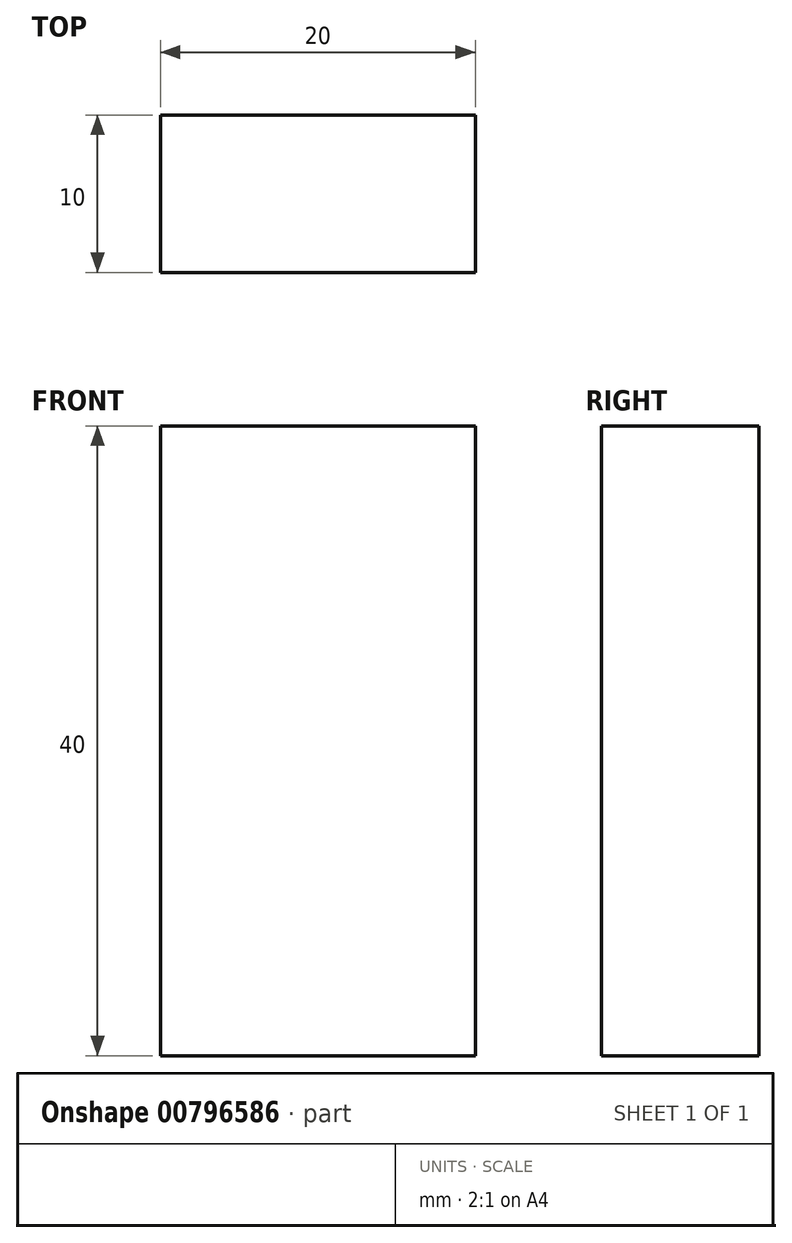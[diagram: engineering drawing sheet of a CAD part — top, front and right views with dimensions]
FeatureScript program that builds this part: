
annotation { "Feature Type Name" : "Feature", "Feature Type Description" : "" }
export const myFeature = defineFeature(function(context is Context, id is Id, definition is map)
    precondition{}
    {
        {
            var Q0;
            Q0=qCreatedBy(makeId("Front.planeOp"),FACE);
            var sketch = newSketch(context, id + "F0", { "sketchPlane" : qUnion([Q0])});
            skLineSegment(sketch, "E0.bottom", {"start": v(10, 20) * mm, "end": v(-10, 20) * mm});
            skLineSegment(sketch, "E0.top", {"start": v(10, -20) * mm, "end": v(-10, -20) * mm});
            skLineSegment(sketch, "E0.left", {"start": v(10, 20) * mm, "end": v(10, -20) * mm});
            skLineSegment(sketch, "E0.right", {"start": v(-10, 20) * mm, "end": v(-10, -20) * mm});
            skPoint(sketch, "E0.middle", {"position": v(0, 0) * mm});
            skSolve(sketch);
        }
        {
            var Q0;
            Q0 = qSketchRegion(id + "F0", true);
            extrude(context, id + "F1", {"entities" : qUnion([Q0]), "depth" : 10 * mm, "offsetDistance" : 25 * mm});
        }
    });
